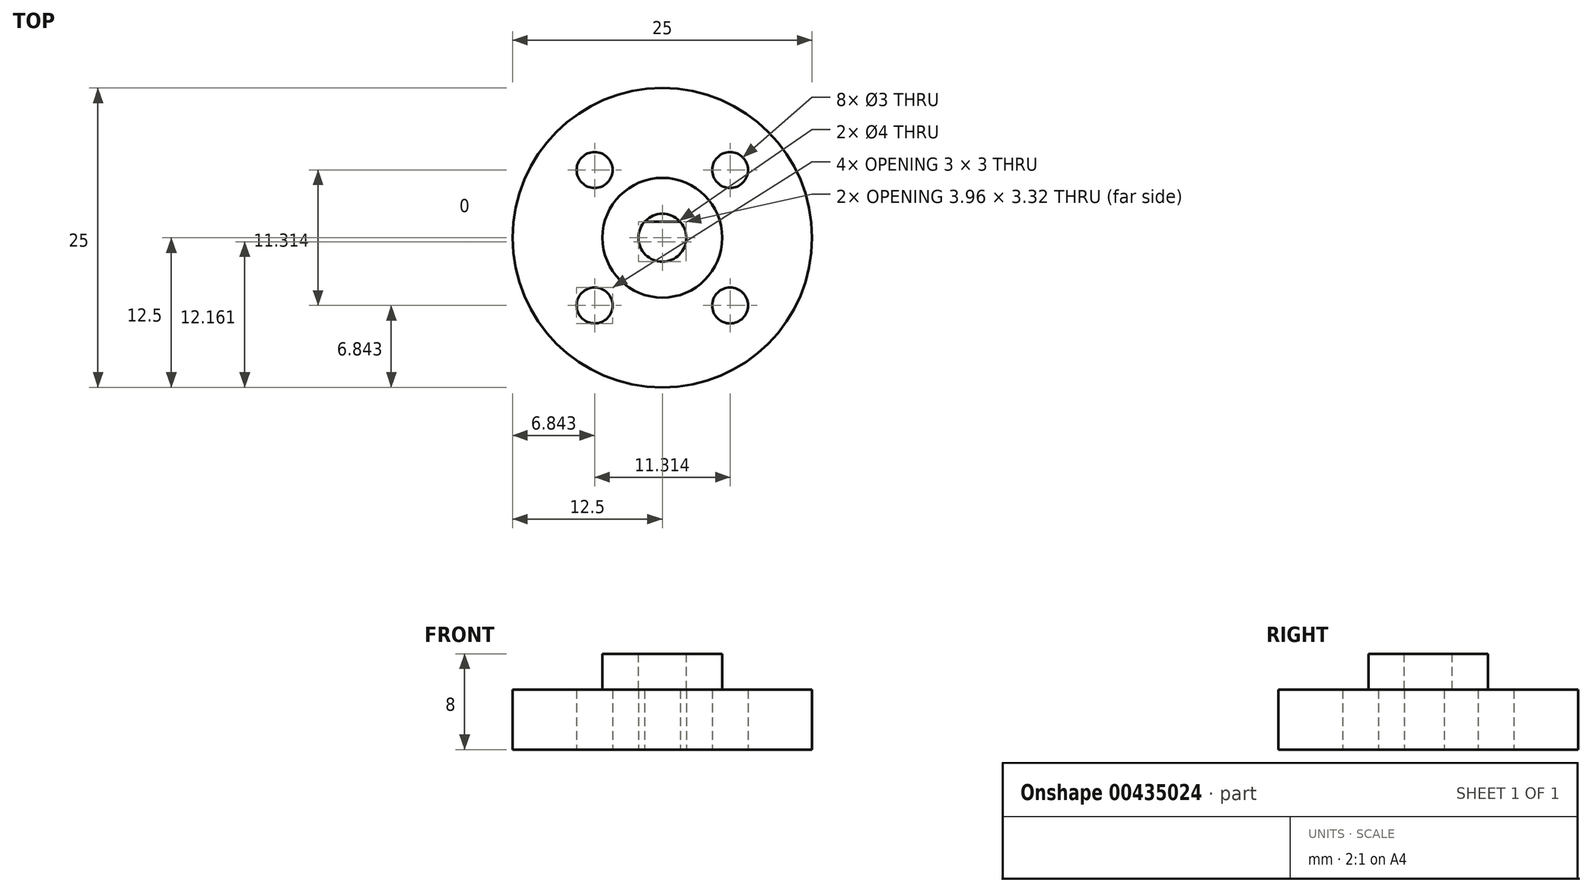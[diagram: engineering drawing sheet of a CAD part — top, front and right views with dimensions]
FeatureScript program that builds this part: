
annotation { "Feature Type Name" : "Feature", "Feature Type Description" : "" }
export const myFeature = defineFeature(function(context is Context, id is Id, definition is map)
    precondition{}
    {
        {
            var Q0;
            Q0=qCreatedBy(makeId("Top.planeOp"),FACE);
            var sketch = newSketch(context, id + "F0", { "sketchPlane" : qUnion([Q0])});
            skCircle(sketch, "E0", {"center": v(0, 0) * mm, "radius": 12.5 * mm});
            skSolve(sketch);
        }
        {
            var Q0;
            Q0=makeQuery(id+"F0.imprint","IMPRINT",FACE,{"disambiguationData":[TD([[makeQuery(id+"F0.imprint","IMPRINT",EDGE,{"derivedFrom":sQuery(id+"F0.wireOp",EDGE,"E0")}),1.0]])]});
            extrude(context, id + "F1", {"entities" : qUnion([Q0]), "depth" : 5 * mm});
        }
        {
            var Q0;
            Q0=makeQuery(id+"F1.opExtrude","CAP_FACE",FACE,{"disambiguationData":[OSD([sQuery(id+"F0.wireOp",EDGE,"E0")])],"isStart":false});
            var sketch = newSketch(context, id + "F2", { "sketchPlane" : qUnion([Q0])});
            skCircle(sketch, "E1", {"center": v(0, 0) * mm, "radius": 5 * mm});
            skSolve(sketch);
        }
        {
            var Q0;
            Q0=makeQuery(id+"F2.imprint","IMPRINT",FACE,{"disambiguationData":[TD([[makeQuery(id+"F2.imprint","IMPRINT",EDGE,{"derivedFrom":sQuery(id+"F2.wireOp",EDGE,"E1")}),1.0]])]});
            extrude(context, id + "F3", {"entities" : qUnion([Q0]), "depth" : 3 * mm});
        }
        {
            var Q0;
            Q0=makeQuery(id+"F3.opExtrude","CAP_FACE",FACE,{"disambiguationData":[OSD([sQuery(id+"F2.wireOp",EDGE,"E1")])],"isStart":false});
            var sketch = newSketch(context, id + "F4", { "sketchPlane" : qUnion([Q0])});
            skCircle(sketch, "E2", {"center": v(0, 0) * mm, "radius": 2 * mm});
            skSolve(sketch);
        }
        {
            var Q0;
            Q0 = qSketchRegion(id + "F4", true);
            extrude(context, id + "F5", {"entities" : qUnion([Q0]), "operationType" : NewBodyOperationType.REMOVE, "oppositeDirection" : true, "depth" : 3 * mm});
        }
        {
            var Q0;
            Q0=makeQuery(id+"F1.opExtrude","CAP_FACE",FACE,{"disambiguationData":[OSD([sQuery(id+"F0.wireOp",EDGE,"E0")])],"isStart":true});
            var sketch = newSketch(context, id + "F6", { "sketchPlane" : qUnion([Q0])});
            skArc(sketch, "E3", {"start": v(1.5, -1.32) * mm, "mid": v(0, 2) * mm, "end": v(-1.5, -1.32) * mm});
            skLineSegment(sketch, "E4", {"start": v(1.5, -1.32) * mm, "end": v(-1.5, -1.32) * mm});
            skSolve(sketch);
        }
        {
            var Q0;
            Q0=makeQuery(id+"F6.imprint","IMPRINT",FACE,{"disambiguationData":[TD([[makeQuery(id+"F6.imprint","IMPRINT",EDGE,{"derivedFrom":sQuery(id+"F6.wireOp",EDGE,"E3")}),1.0]])]});
            extrude(context, id + "F7", {"entities" : qUnion([Q0]), "operationType" : NewBodyOperationType.REMOVE, "oppositeDirection" : true, "depth" : 25 * mm});
        }
        {
            var Q0;
            Q0=makeQuery(id+"F1.opExtrude","CAP_FACE",FACE,{"disambiguationData":[OSD([sQuery(id+"F0.wireOp",EDGE,"E0")])],"isStart":true});
            var sketch = newSketch(context, id + "F8", { "sketchPlane" : qUnion([Q0])});
            skCircle(sketch, "E5", {"center": v(-5.66, -5.66) * mm, "radius": 1.5 * mm});
            skCircle(sketch, "E6.1.0", {"center": v(5.66, -5.66) * mm, "radius": 1.5 * mm});
            skCircle(sketch, "E6.2.0", {"center": v(5.66, 5.66) * mm, "radius": 1.5 * mm});
            skCircle(sketch, "E6.3.0", {"center": v(-5.66, 5.66) * mm, "radius": 1.5 * mm});
            skPoint(sketch, "E6.center", {"position": v(0, 0) * mm});
            skLineSegment(sketch, "E7", {"start": v(0, 0) * mm, "end": v(0, -12.5) * mm, "construction": true});
            skPoint(sketch, "E7.endSnap0", {"position": v(0, -2) * mm});
            skLineSegment(sketch, "E8", {"start": v(0, 0) * mm, "end": v(-8.84, -8.84) * mm, "construction": true});
            skSolve(sketch);
        }
        {
            var Q0;
            Q0=makeQuery(id+"F8.imprint","IMPRINT",FACE,{"disambiguationData":[TD([[makeQuery(id+"F8.imprint","IMPRINT",EDGE,{"derivedFrom":sQuery(id+"F8.wireOp",EDGE,"E6.3.0")}),1.0]])]});
            var Q1;
            Q1=makeQuery(id+"F8.imprint","IMPRINT",FACE,{"disambiguationData":[TD([[makeQuery(id+"F8.imprint","IMPRINT",EDGE,{"derivedFrom":sQuery(id+"F8.wireOp",EDGE,"E5")}),1.0]])]});
            var Q2;
            Q2=makeQuery(id+"F8.imprint","IMPRINT",FACE,{"disambiguationData":[TD([[makeQuery(id+"F8.imprint","IMPRINT",EDGE,{"derivedFrom":sQuery(id+"F8.wireOp",EDGE,"E6.1.0")}),1.0]])]});
            var Q3;
            Q3=makeQuery(id+"F8.imprint","IMPRINT",FACE,{"disambiguationData":[TD([[makeQuery(id+"F8.imprint","IMPRINT",EDGE,{"derivedFrom":sQuery(id+"F8.wireOp",EDGE,"E6.2.0")}),1.0]])]});
            extrude(context, id + "F9", {"entities" : qUnion([Q0, Q1, Q2, Q3]), "operationType" : NewBodyOperationType.REMOVE, "oppositeDirection" : true, "depth" : 25 * mm});
        }
    });
